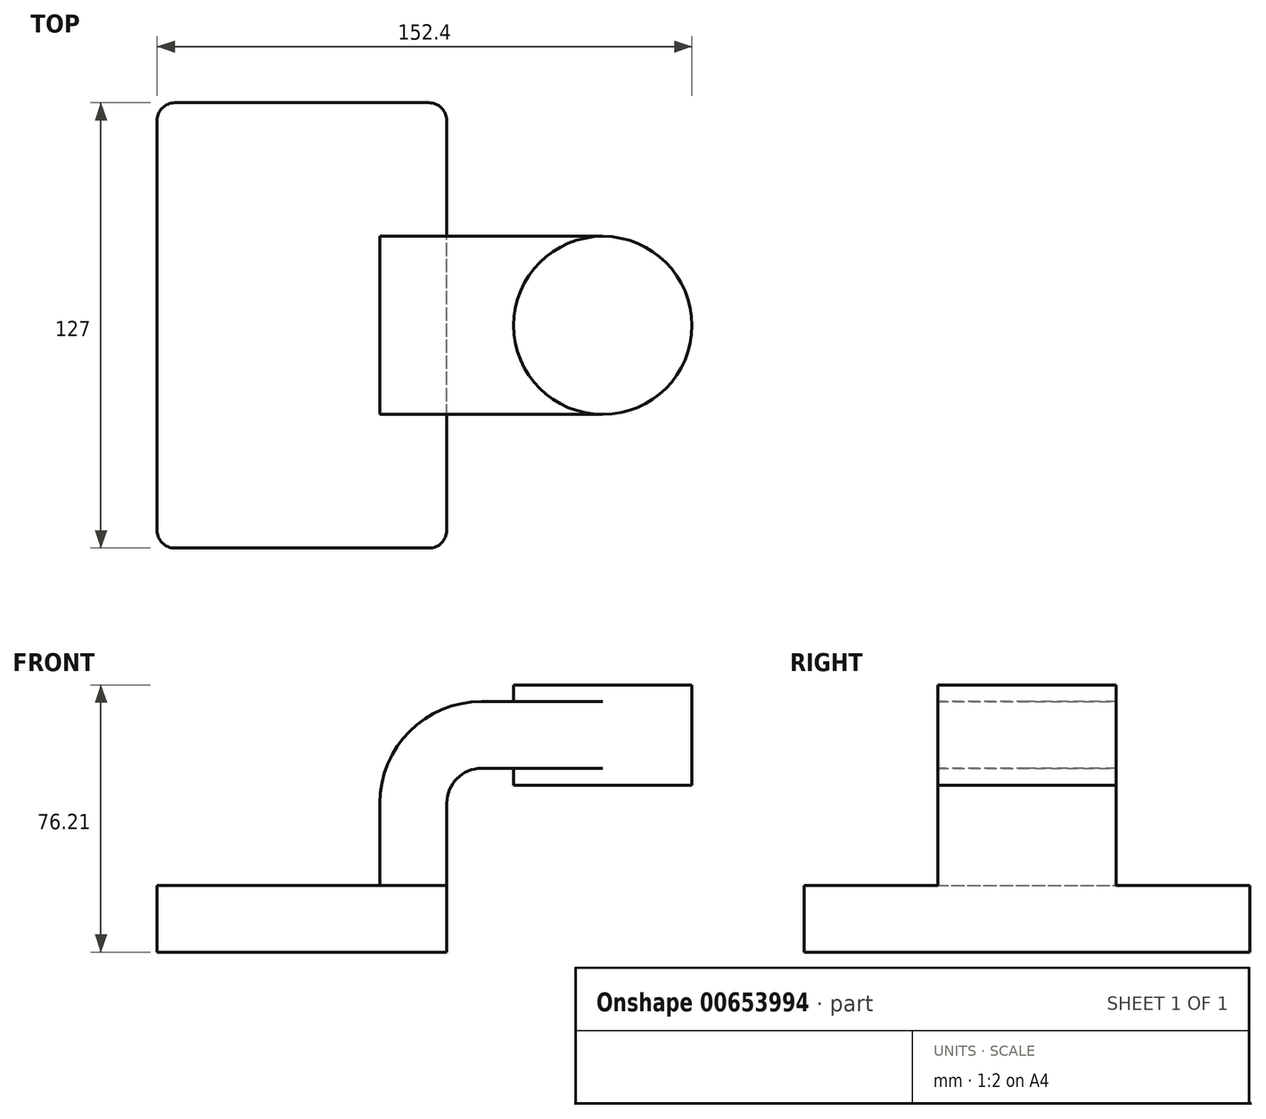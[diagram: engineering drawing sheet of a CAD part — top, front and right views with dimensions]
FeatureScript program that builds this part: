
annotation { "Feature Type Name" : "Feature", "Feature Type Description" : "" }
export const myFeature = defineFeature(function(context is Context, id is Id, definition is map)
    precondition{}
    {
        {
            var Q0;
            Q0=qCreatedBy(makeId("Front.planeOp"),FACE);
            var sketch = newSketch(context, id + "F0", { "sketchPlane" : qUnion([Q0])});
            skLineSegment(sketch, "E0.bottom", {"start": v(41.27, 9.53) * mm, "end": v(-41.28, 9.53) * mm});
            skLineSegment(sketch, "E0.top", {"start": v(41.28, -9.52) * mm, "end": v(-41.28, -9.52) * mm});
            skLineSegment(sketch, "E0.left", {"start": v(41.28, 9.53) * mm, "end": v(41.28, -9.52) * mm});
            skLineSegment(sketch, "E0.right", {"start": v(-41.28, 9.53) * mm, "end": v(-41.28, -9.52) * mm});
            skPoint(sketch, "E0.middle", {"position": v(0, 0) * mm});
            skLineSegment(sketch, "E1", {"start": v(41.27, 9.53) * mm, "end": v(41.27, 32.96) * mm});
            skArc(sketch, "E2", {"start": v(41.27, 32.96) * mm, "mid": v(44.18, 39.97) * mm, "end": v(51.19, 42.88) * mm});
            skLineSegment(sketch, "E3", {"start": v(51.19, 42.88) * mm, "end": v(85.73, 42.88) * mm});
            skLineSegment(sketch, "E4.bottom", {"start": v(111.12, 66.68) * mm, "end": v(60.32, 66.68) * mm});
            skLineSegment(sketch, "E4.top", {"start": v(111.12, 38.1) * mm, "end": v(60.33, 38.1) * mm});
            skLineSegment(sketch, "E4.left", {"start": v(111.12, 66.68) * mm, "end": v(111.12, 38.1) * mm});
            skLineSegment(sketch, "E4.right", {"start": v(60.32, 66.68) * mm, "end": v(60.33, 38.1) * mm});
            skPoint(sketch, "E4.middle", {"position": v(85.72, 52.39) * mm});
            skLineSegment(sketch, "E5.0", {"start": v(51.19, 61.93) * mm, "end": v(85.73, 61.93) * mm});
            skArc(sketch, "E5.1", {"start": v(22.22, 32.96) * mm, "mid": v(30.7, 53.44) * mm, "end": v(51.19, 61.93) * mm});
            skLineSegment(sketch, "E5.2", {"start": v(22.22, 9.53) * mm, "end": v(22.22, 32.96) * mm});
            skLineSegment(sketch, "E6", {"start": v(85.72, 38.1) * mm, "end": v(85.72, 66.68) * mm});
            skFitSpline(sketch, "E7", {"points": [v(-41.28, 9.52) * mm, v(51.19, 61.93) * mm], "startDerivative": vector(0, 96.04) * mm, "endDerivative": vector(125.94, 0) * mm});
            skPoint(sketch, "E8", {"position": v(68.46, 61.93) * mm});
            skSolve(sketch);
        }
        {
            var Q0;
            Q0=makeQuery(id+"F0.imprint","IMPRINT",FACE,{"disambiguationData":[TD([[makeQuery(id+"F0.imprint","IMPRINT",EDGE,{"derivedFrom":sQuery(id+"F0.wireOp",EDGE,"E0.top")}),-1.0]])]});
            extrude(context, id + "F1", {"entities" : qUnion([Q0]), "endBound" : BoundingType.SYMMETRIC, "depth" : 127 * mm, "offsetDistance" : 25.4 * mm});
        }
        {
            var Q0;
            {var subQ7=sQuery(id+"F0.wireOp",EDGE,"E1");Q0=makeQuery(id+"F0.imprint","IMPRINT",FACE,{"disambiguationData":[TD([[makeQuery(id+"F0.imprint","IMPRINT",EDGE,{"derivedFrom":subQ7}),1.0]])]});}
            var Q1;
            {var subQ0=sQuery(id+"F0.wireOp",EDGE,"E6");var subQ1=sQuery(id+"F0.wireOp",EDGE,"E3");var subQ2=makeQuery(id+"F0.imprint","INTERSECT",VERTEX,{"derivedFrom":[subQ1,subQ0]});Q1=makeQuery(id+"F0.imprint","IMPRINT",FACE,{"disambiguationData":[TD([[makeQuery(id+"F0.imprint","IMPRINT",EDGE,{"disambiguationData":[TD([[subQ2,1.0]])],"derivedFrom":subQ1}),1.0]])]});}
            extrude(context, id + "F2", {"entities" : qUnion([Q0, Q1]), "operationType" : NewBodyOperationType.ADD, "endBound" : BoundingType.SYMMETRIC, "depth" : 50.8 * mm, "offsetDistance" : 25.4 * mm});
        }
        {
            var Q0;
            Q0=makeQuery(id+"F0.imprint","IMPRINT",FACE,{"disambiguationData":[TD([[makeQuery(id+"F0.imprint","IMPRINT",EDGE,{"derivedFrom":sQuery(id+"F0.wireOp",EDGE,"E5.1")}),1.0]])]});
            extrude(context, id + "F3", {"entities" : qUnion([Q0]), "operationType" : NewBodyOperationType.ADD, "endBound" : BoundingType.SYMMETRIC, "depth" : 15.88 * mm, "offsetDistance" : 25.4 * mm});
        }
        {
            var Q0;
            {var subQ0=sQuery(id+"F0.wireOp",EDGE,"E4.left");Q0=makeQuery(id+"F0.imprint","IMPRINT",FACE,{"disambiguationData":[TD([[makeQuery(id+"F0.imprint","IMPRINT",EDGE,{"derivedFrom":subQ0}),-1.0]])]});}
            var Q1;
            Q1=sQuery(id+"F0.wireOp",EDGE,"E6");
            revolve(context, id + "F4", {"operationType" : NewBodyOperationType.ADD, "entities" : qUnion([Q0]), "axis" : qUnion([Q1]), "revolveType" : RevolveType.FULL});
        }
        {
            var Q0;
            Q0=makeQuery(id+"F1.opExtrude","CAP_EDGE",EDGE,{"disambiguationData":[OSD([sQuery(id+"F0.wireOp",EDGE,"E0.right")])],"isStart":false});
            var Q1;
            Q1=makeQuery(id+"F1.opExtrude","CAP_EDGE",EDGE,{"disambiguationData":[OSD([sQuery(id+"F0.wireOp",EDGE,"E0.left")])],"isStart":false});
            var Q2;
            Q2=makeQuery(id+"F1.opExtrude","CAP_EDGE",EDGE,{"disambiguationData":[OSD([sQuery(id+"F0.wireOp",EDGE,"E0.right")])],"isStart":true});
            var Q3;
            Q3=makeQuery(id+"F1.opExtrude","CAP_EDGE",EDGE,{"disambiguationData":[OSD([sQuery(id+"F0.wireOp",EDGE,"E0.left")])],"isStart":true});
            fillet(context, id + "F5", {"entities" : qUnion([Q0, Q1, Q2, Q3]), "radius" : 5.08 * mm, "tangentPropagation" : true, "allowEdgeOverflow" : false});
        }
    });
